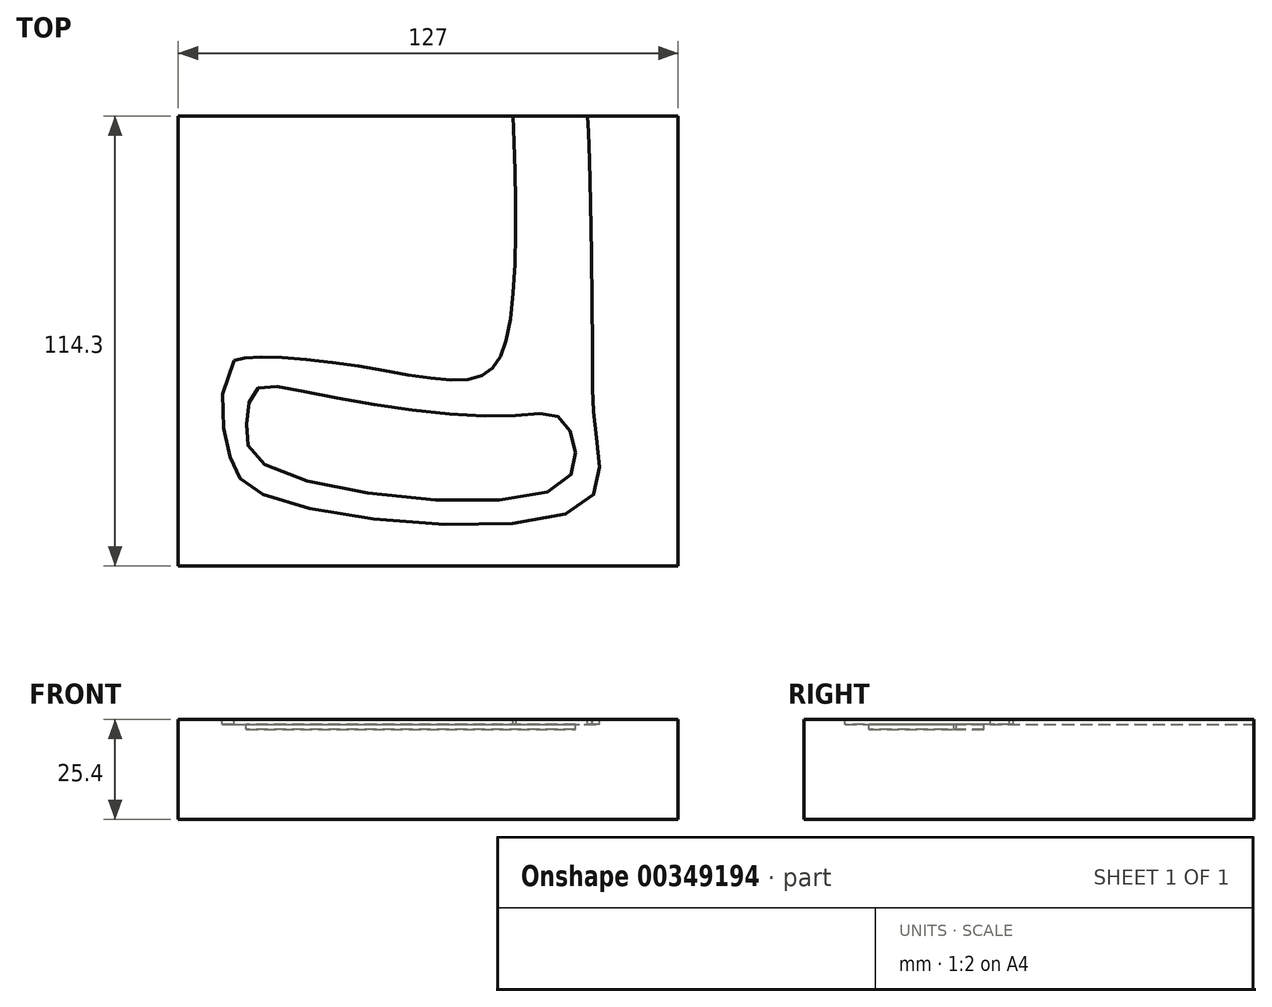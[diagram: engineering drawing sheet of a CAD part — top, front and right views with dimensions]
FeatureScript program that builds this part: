
annotation { "Feature Type Name" : "Feature", "Feature Type Description" : "" }
export const myFeature = defineFeature(function(context is Context, id is Id, definition is map)
    precondition{}
    {
        {
            var Q0;
            Q0=qCreatedBy(makeId("Top.planeOp"),FACE);
            var sketch = newSketch(context, id + "F0", { "sketchPlane" : qUnion([Q0])});
            skLineSegment(sketch, "E0", {"start": v(0, 0) * mm, "end": v(0, 114.3) * mm});
            skLineSegment(sketch, "E1", {"start": v(0, 114.3) * mm, "end": v(127, 114.3) * mm});
            skLineSegment(sketch, "E2", {"start": v(127, 114.3) * mm, "end": v(127, 0) * mm});
            skLineSegment(sketch, "E3", {"start": v(127, 0) * mm, "end": v(0, 0) * mm});
            skSolve(sketch);
        }
        {
            var Q0;
            Q0 = qSketchRegion(id + "F0", true);
            extrude(context, id + "F1", {"entities" : qUnion([Q0]), "depth" : 25.4 * mm});
        }
        {
            var Q0;
            Q0=makeQuery(id+"F1.opExtrude","CAP_FACE",FACE,{"disambiguationData":[OSD([sQuery(id+"F0.wireOp",EDGE,"E0"),sQuery(id+"F0.wireOp",EDGE,"E1"),sQuery(id+"F0.wireOp",EDGE,"E2"),sQuery(id+"F0.wireOp",EDGE,"E3")])],"isStart":false});
            var sketch = newSketch(context, id + "F2", { "sketchPlane" : qUnion([Q0])});
            skFitSpline(sketch, "E4", {"points": [v(14.18, 52.2) * mm, v(12.97, 28.49) * mm, v(23.03, 17.57) * mm, v(102.15, 14.9) * mm, v(106.41, 31.51) * mm, v(105.23, 45.25) * mm, v(105.23, 56.63) * mm, v(104.4, 104.15) * mm, v(103.93, 114.3) * mm], "startDerivative": vector(-115.83, -188.07) * mm, "endDerivative": vector(-8.62, 80.33) * mm});
            skFitSpline(sketch, "E5", {"points": [v(14.18, 52.2) * mm, v(42.47, 51.26) * mm, v(75.35, 47.74) * mm, v(83.67, 58.76) * mm, v(85.09, 114.3) * mm], "startDerivative": vector(40.94, 18.84) * mm, "endDerivative": vector(-6.36, 138.77) * mm});
            skSolve(sketch);
        }
        {
            var Q0;
            {var subQ0=sQuery(id+"F2.wireOp",EDGE,"E4");Q0=makeQuery(id+"F2.imprint","IMPRINT",FACE,{"disambiguationData":[TD([[makeQuery(id+"F2.imprint","IMPRINT",EDGE,{"derivedFrom":subQ0}),1.0]])]});}
            extrude(context, id + "F3", {"entities" : qUnion([Q0]), "operationType" : NewBodyOperationType.REMOVE, "oppositeDirection" : true, "depth" : 1.27 * mm});
        }
        {
            var Q0;
            Q0=makeQuery(id+"F3.boolean.opBoolean","COPY",FACE,{"derivedFrom":makeQuery(id+"F3.opExtrude","CAP_FACE",FACE,{"disambiguationData":[OSD([sQuery(id+"F0.wireOp",EDGE,"E1"),sQuery(id+"F2.wireOp",EDGE,"E4"),sQuery(id+"F2.wireOp",EDGE,"E5")])],"isStart":false})});
            var sketch = newSketch(context, id + "F4", { "sketchPlane" : qUnion([Q0])});
            skPoint(sketch, "E6", {"position": v(28.2, 34.47) * mm});
            skPoint(sketch, "E7", {"position": v(92.33, 29.72) * mm});
            skFitSpline(sketch, "E8", {"points": [v(17.33, 36) * mm, v(22.03, 25.72) * mm, v(94.93, 19.24) * mm, v(100.74, 30.2) * mm, v(96.55, 37.91) * mm, v(86.2, 38.25) * mm, v(59, 39.7) * mm, v(29.79, 44.75) * mm, v(19.57, 44.73) * mm, v(17.33, 36) * mm]});
            skSolve(sketch);
        }
        {
            var Q0;
            Q0=makeQuery(id+"F4.imprint","IMPRINT",FACE,{"disambiguationData":[TD([[makeQuery(id+"F4.imprint","IMPRINT",EDGE,{"derivedFrom":sQuery(id+"F4.wireOp",EDGE,"E8")}),1.0]])]});
            var Q1;
            Q1=sQuery(id+"F4.wireOp",EDGE,"E8");
            extrude(context, id + "F5", {"entities" : qUnion([Q0]), "operationType" : NewBodyOperationType.REMOVE, "surfaceEntities" : qUnion([Q1]), "oppositeDirection" : true, "depth" : 1.27 * mm});
        }
    });
